# Revit family: Gamme Turia 1V - Applique
name_source: partatom
category: Portes
units: mm (PartAtom-declared; Revit-internal decimal feet)

## family parameters
Basée sur le plan de construction = Non
Couper avec des vides une fois chargée = Non
Partagée = Non
Repère de localisation dans la pièce = Non
Toujours verticalement = Oui

## types (8) — shared parameters
Construction analytique = <Aucun>
Définir les propriétés thermiques par = Type schématique
Hauteur Réservation = 2178 mm  [stored 7.14567 ft]
zero-valued in all types: Elévation par défaut

## per-type parameters (varying)
| type | Code d'assemblage | Côte_passage_libre_90 | Fabricant | Hauteur brute | Largeur Réservation | Largeur brute | Modèle |
| Turia_1V - 900 x 2178 | B2030 | 937 mm |  | 0 mm  [stored 0 ft] | 1056 mm  [stored 3.46457 ft] | 0 mm  [stored 0 ft] |  |
| Turia_1V - 1000 x 2178 |  | 1037 mm |  | 0 mm  [stored 0 ft] | 1156 mm | 0 mm  [stored 0 ft] |  |
| Turia_1V - 1100 x 2178 |  | 937 mm |  | 0 mm  [stored 0 ft] | 1056 mm  [stored 3.46457 ft] | 0 mm  [stored 0 ft] |  |
| Neo_1V - 900 x 2178 | B2030 | 937 mm |  | 0 mm  [stored 0 ft] | 1056 mm  [stored 3.46457 ft] | 0 mm  [stored 0 ft] |  |
| TURIA_1V - 900 x 2179 | B2030 | 937 mm |  | 0 mm  [stored 0 ft] | 1056 mm  [stored 3.46457 ft] | 0 mm  [stored 0 ft] |  |
| TURIA_1V -1346*2178 | B2030 | 1227 mm | PORTEMETAL | 2178 mm  [stored 7.14567 ft] | 1346 mm | 1346 mm | TURIA |
| NEO_1V -1346*2178 | B2030 | 1227 mm | PORTEMETAL | 2178 mm  [stored 7.14567 ft] | 1346 mm | 1346 mm | NEO |
| TURIA_1V - 1046*2178 | B2030 | 927 mm | PORTEMETAL | 2178 mm  [stored 7.14567 ft] | 1046 mm | 1046 mm | TURIA |

note: [stored X ft] marks values corroborated as IEEE doubles in the binary element streams (Revit-internal decimal feet)
